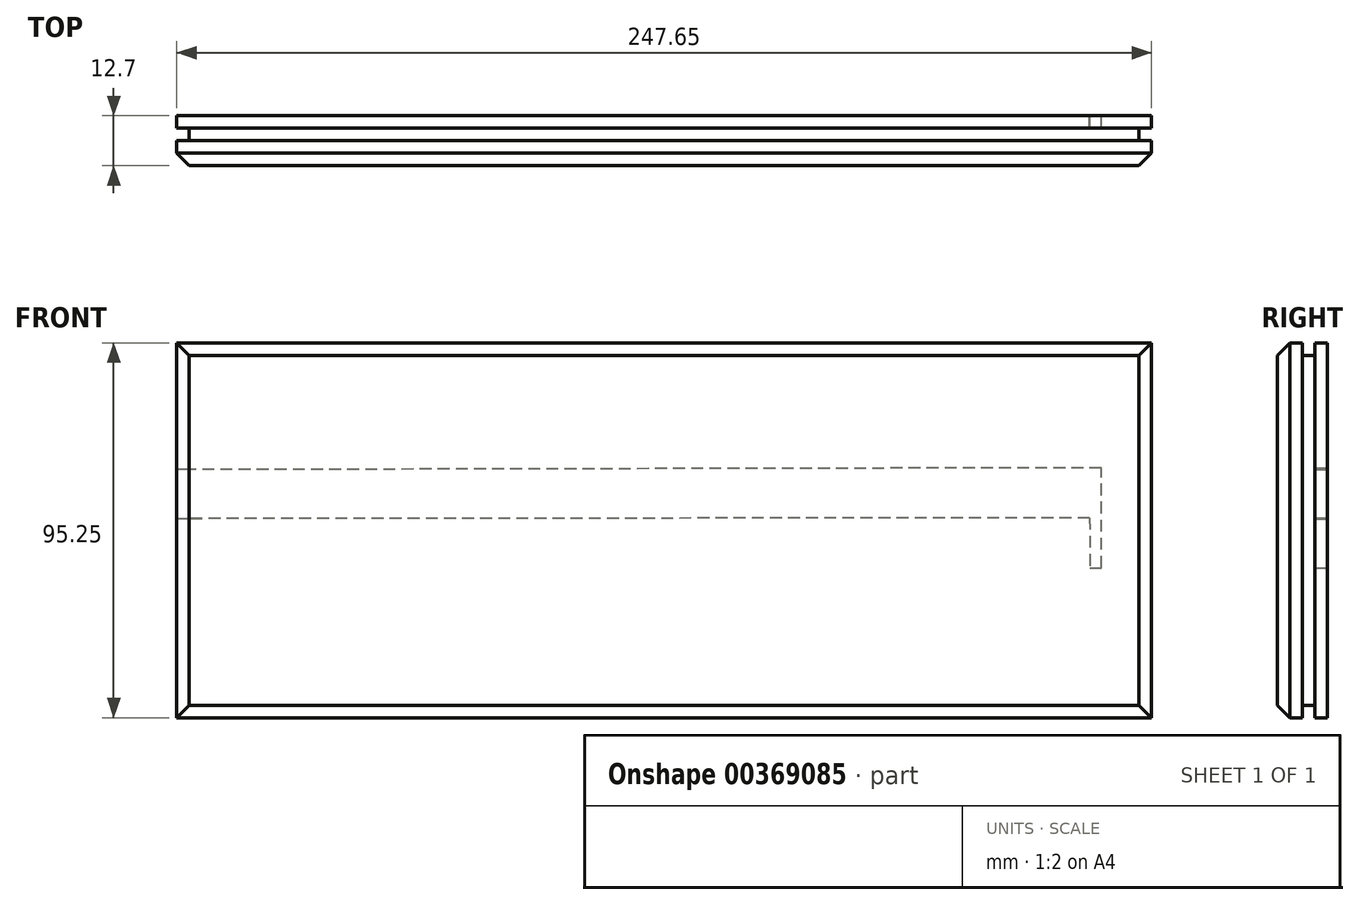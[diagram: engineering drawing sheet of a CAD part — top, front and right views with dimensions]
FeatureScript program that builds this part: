
annotation { "Feature Type Name" : "Feature", "Feature Type Description" : "" }
export const myFeature = defineFeature(function(context is Context, id is Id, definition is map)
    precondition{}
    {
        {
            var Q0;
            Q0=qCreatedBy(makeId("Front.planeOp"),FACE);
            var sketch = newSketch(context, id + "F0", { "sketchPlane" : qUnion([Q0])});
            skLineSegment(sketch, "E0.bottom", {"start": v(-31.8, 0) * mm, "end": v(215.84, 0) * mm});
            skLineSegment(sketch, "E0.top", {"start": v(-31.8, 95.25) * mm, "end": v(215.84, 95.25) * mm});
            skLineSegment(sketch, "E0.left", {"start": v(-31.8, 0) * mm, "end": v(-31.8, 95.25) * mm});
            skLineSegment(sketch, "E0.right", {"start": v(215.84, 0) * mm, "end": v(215.84, 95.25) * mm});
            skSolve(sketch);
        }
        {
            var Q0;
            Q0 = qSketchRegion(id + "F0", true);
            extrude(context, id + "F1", {"entities" : qUnion([Q0]), "depth" : 6.35 * mm});
        }
        {
            var Q0;
            Q0=makeQuery(id+"F1.opExtrude","CAP_EDGE",EDGE,{"disambiguationData":[OSD([sQuery(id+"F0.wireOp",EDGE,"E0.top")])],"isStart":false});
            var Q1;
            Q1=makeQuery(id+"F1.opExtrude","CAP_EDGE",EDGE,{"disambiguationData":[OSD([sQuery(id+"F0.wireOp",EDGE,"E0.left")])],"isStart":false});
            var Q2;
            Q2=makeQuery(id+"F1.opExtrude","CAP_EDGE",EDGE,{"disambiguationData":[OSD([sQuery(id+"F0.wireOp",EDGE,"E0.bottom")])],"isStart":false});
            var Q3;
            Q3=makeQuery(id+"F1.opExtrude","CAP_EDGE",EDGE,{"disambiguationData":[OSD([sQuery(id+"F0.wireOp",EDGE,"E0.right")])],"isStart":false});
            chamfer(context, id + "F2", {"entities" : qUnion([Q0, Q1, Q2, Q3]), "width" : 3.17 * mm, "tangentPropagation" : true});
        }
        {
            var Q0;
            Q0=makeQuery(id+"F1.opExtrude","CAP_FACE",FACE,{"disambiguationData":[OSD([sQuery(id+"F0.wireOp",EDGE,"E0.bottom"),sQuery(id+"F0.wireOp",EDGE,"E0.top"),sQuery(id+"F0.wireOp",EDGE,"E0.left"),sQuery(id+"F0.wireOp",EDGE,"E0.right")])],"isStart":true});
            var sketch = newSketch(context, id + "F3", { "sketchPlane" : qUnion([Q0])});
            skLineSegment(sketch, "E1.0", {"start": v(28.63, 92.08) * mm, "end": v(-212.67, 92.08) * mm});
            skLineSegment(sketch, "E1.1", {"start": v(28.63, 3.17) * mm, "end": v(28.63, 92.08) * mm});
            skLineSegment(sketch, "E1.2", {"start": v(28.63, 3.17) * mm, "end": v(-212.67, 3.17) * mm});
            skLineSegment(sketch, "E1.3", {"start": v(-212.67, 3.17) * mm, "end": v(-212.67, 92.08) * mm});
            skSolve(sketch);
        }
        {
            var Q0;
            Q0 = qSketchRegion(id + "F3", true);
            extrude(context, id + "F4", {"entities" : qUnion([Q0]), "operationType" : NewBodyOperationType.ADD, "depth" : 3.17 * mm});
        }
        {
            var Q0;
            Q0=makeQuery(id+"F4.opExtrude","CAP_FACE",FACE,{"disambiguationData":[OSD([sQuery(id+"F3.wireOp",EDGE,"E1.0"),sQuery(id+"F3.wireOp",EDGE,"E1.1"),sQuery(id+"F3.wireOp",EDGE,"E1.2"),sQuery(id+"F3.wireOp",EDGE,"E1.3")])],"isStart":false});
            var sketch = newSketch(context, id + "F5", { "sketchPlane" : qUnion([Q0])});
            skLineSegment(sketch, "E2.0", {"start": v(31.8, 95.25) * mm, "end": v(-215.84, 95.25) * mm});
            skLineSegment(sketch, "E2.1", {"start": v(31.8, 0) * mm, "end": v(31.8, 95.25) * mm});
            skLineSegment(sketch, "E2.2", {"start": v(31.8, 0) * mm, "end": v(-215.84, 0) * mm});
            skLineSegment(sketch, "E2.3", {"start": v(-215.84, 0) * mm, "end": v(-215.84, 95.25) * mm});
            skSolve(sketch);
        }
        {
            var Q0;
            Q0 = qSketchRegion(id + "F5", true);
            extrude(context, id + "F6", {"entities" : qUnion([Q0]), "operationType" : NewBodyOperationType.ADD, "depth" : 3.17 * mm});
        }
        {
            var Q0;
            Q0=makeQuery(id+"F6.opExtrude","CAP_FACE",FACE,{"disambiguationData":[OSD([sQuery(id+"F5.wireOp",EDGE,"E2.0"),sQuery(id+"F5.wireOp",EDGE,"E2.1"),sQuery(id+"F5.wireOp",EDGE,"E2.2"),sQuery(id+"F5.wireOp",EDGE,"E2.3")])],"isStart":false});
            var sketch = newSketch(context, id + "F7", { "sketchPlane" : qUnion([Q0])});
            skPoint(sketch, "E3", {"position": v(-203.14, 63.5) * mm});
            skLineSegment(sketch, "E4.0", {"start": v(-200.2, 63.5) * mm, "end": v(-203.14, 63.5) * mm});
            skLineSegment(sketch, "E5", {"start": v(-200.1, 50.8) * mm, "end": v(31.8, 50.56) * mm});
            skLineSegment(sketch, "E6", {"start": v(-203.14, 38.1) * mm, "end": v(-203.14, 63.5) * mm});
            skLineSegment(sketch, "E7.MirrorCS", {"start": v(-200.1, 50.8) * mm, "end": v(-200.24, 38.1) * mm});
            skLineSegment(sketch, "E8.MirrorCS", {"start": v(-203.12, 63.5) * mm, "end": v(-203.17, 38.1) * mm});
            skLineSegment(sketch, "E9.MirrorCS", {"start": v(-203.12, 63.5) * mm, "end": v(31.83, 63.02) * mm});
            skLineSegment(sketch, "E10.MirrorCS", {"start": v(-200.24, 38.1) * mm, "end": v(-203.17, 38.1) * mm});
            skSolve(sketch);
        }
        {
            var Q0;
            Q0=makeQuery(id+"F7.imprint","IMPRINT",FACE,{"disambiguationData":[TD([[makeQuery(id+"F7.imprint","IMPRINT",EDGE,{"derivedFrom":sQuery(id+"F7.wireOp",EDGE,"E4.0")}),1.0]])]});
            var Q1;
            {var subQ4=sQuery(id+"F7.wireOp",EDGE,"E5");Q1=makeQuery(id+"F7.imprint","IMPRINT",FACE,{"disambiguationData":[TD([[makeQuery(id+"F7.imprint","IMPRINT",EDGE,{"derivedFrom":subQ4}),1.0]])]});}
            extrude(context, id + "F8", {"entities" : qUnion([Q0, Q1]), "operationType" : NewBodyOperationType.REMOVE, "oppositeDirection" : true, "depth" : 3.17 * mm});
        }
    });
